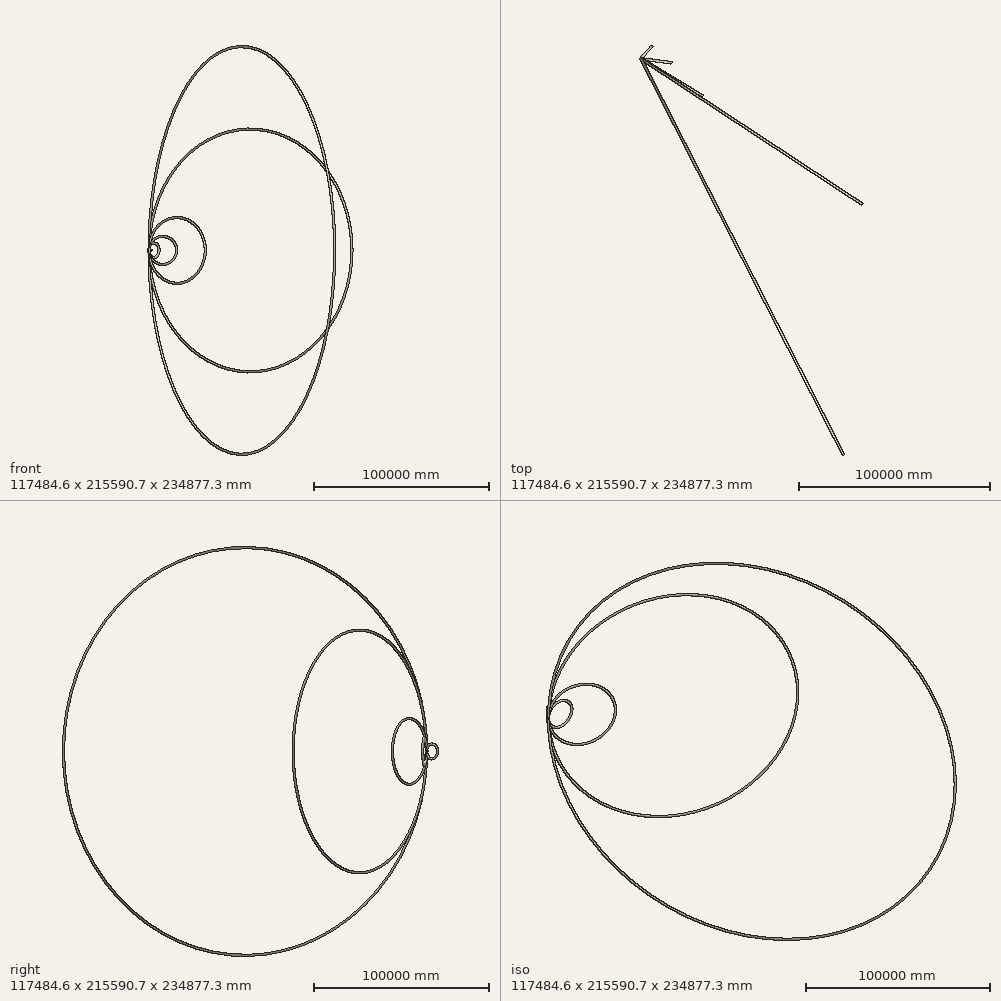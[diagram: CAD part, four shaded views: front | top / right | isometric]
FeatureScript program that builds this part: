
annotation { "Feature Type Name" : "Feature", "Feature Type Description" : "" }
export const myFeature = defineFeature(function(context is Context, id is Id, definition is map)
    precondition{}
    {
        {
            var Q0;
            Q0=qCreatedBy(makeId("Top.planeOp"),FACE);
            var sketch = newSketch(context, id + "F0", { "sketchPlane" : qUnion([Q0])});
            skLineSegment(sketch, "E0", {"start": v(-131.68, -317) * mm, "end": v(58.83, -44.44) * mm});
            skLineSegment(sketch, "E1", {"start": v(107.15, -38.13) * mm, "end": v(337.93, -277.55) * mm});
            skArc(sketch, "E2", {"start": v(107.15, -38.13) * mm, "mid": v(87.87, -78.67) * mm, "end": v(58.83, -44.44) * mm});
            skFitSpline(sketch, "E3", {"points": [v(-131.68, -317) * mm, v(337.93, -277.55) * mm], "startDerivative": vector(425.75, 390.82) * mm, "endDerivative": vector(441.2, 339.46) * mm});
            skLineSegment(sketch, "E4", {"start": v(-582.83, 0) * mm, "end": v(-432.33, -475.47) * mm, "construction": true});
            skLineSegment(sketch, "E5", {"start": v(-131.68, -317) * mm, "end": v(-482.5, -317) * mm, "construction": true});
            skSolve(sketch);
        }
        {
            var Q0;
            Q0 = qSketchRegion(id + "F0", true);
            var Q1;
            Q1=sQuery(id+"F0.wireOp",EDGE,"E4");
            revolve(context, id + "F1", {"surfaceOperationType" : NewSurfaceOperationType.NEW, "entities" : qUnion([Q0]), "axis" : qUnion([Q1]), "revolveType" : RevolveType.FULL});
        }
        {
            var Q0;
            Q0=qCreatedBy(makeId("Top.planeOp"),FACE);
            var sketch = newSketch(context, id + "F2", { "sketchPlane" : qUnion([Q0])});
            skCircle(sketch, "E6", {"center": v(-1397.87, -1019.52) * mm, "radius": 651.66 * mm});
            skLineSegment(sketch, "E7", {"start": v(-674.93, 4057.68) * mm, "end": v(3816.1, 0) * mm, "construction": true});
            skLineSegment(sketch, "E8", {"start": v(7135.37, 2192.65) * mm, "end": v(6077.63, -5637.97) * mm, "construction": true});
            skLineSegment(sketch, "E9", {"start": v(16717.36, -7464.38) * mm, "end": v(12653.7, -14164.2) * mm, "construction": true});
            skLineSegment(sketch, "E10", {"start": v(27427.42, -117445.29) * mm, "end": v(60811.52, -100380.38) * mm, "construction": true});
            skLineSegment(sketch, "E11", {"start": v(54766.77, -42154.56) * mm, "end": v(64547.64, -27283.42) * mm, "construction": true});
            skSolve(sketch);
        }
        {
            var Q0;
            Q0 = qSketchRegion(id + "F2", true);
            var Q1;
            Q1=sQuery(id+"F2.wireOp",EDGE,"E7");
            revolve(context, id + "F3", {"surfaceOperationType" : NewSurfaceOperationType.NEW, "entities" : qUnion([Q0]), "axis" : qUnion([Q1]), "revolveType" : RevolveType.FULL});
        }
        {
            var Q0;
            Q0 = qSketchRegion(id + "F2", true);
            var Q1;
            Q1=sQuery(id+"F2.wireOp",EDGE,"E8");
            revolve(context, id + "F4", {"surfaceOperationType" : NewSurfaceOperationType.NEW, "entities" : qUnion([Q0]), "axis" : qUnion([Q1]), "revolveType" : RevolveType.FULL});
        }
        {
            var Q0;
            Q0 = qSketchRegion(id + "F2", true);
            var Q1;
            Q1=sQuery(id+"F2.wireOp",EDGE,"E9");
            revolve(context, id + "F5", {"surfaceOperationType" : NewSurfaceOperationType.NEW, "entities" : qUnion([Q0]), "axis" : qUnion([Q1]), "revolveType" : RevolveType.FULL});
        }
        {
            var Q0;
            Q0 = qSketchRegion(id + "F2", true);
            var Q1;
            Q1=sQuery(id+"F2.wireOp",EDGE,"E10");
            revolve(context, id + "F6", {"surfaceOperationType" : NewSurfaceOperationType.NEW, "entities" : qUnion([Q0]), "axis" : qUnion([Q1]), "revolveType" : RevolveType.FULL});
        }
        {
            var Q0;
            Q0 = qSketchRegion(id + "F2", true);
            var Q1;
            Q1=sQuery(id+"F2.wireOp",EDGE,"E11");
            revolve(context, id + "F7", {"surfaceOperationType" : NewSurfaceOperationType.NEW, "entities" : qUnion([Q0]), "axis" : qUnion([Q1]), "revolveType" : RevolveType.FULL});
        }
    });
